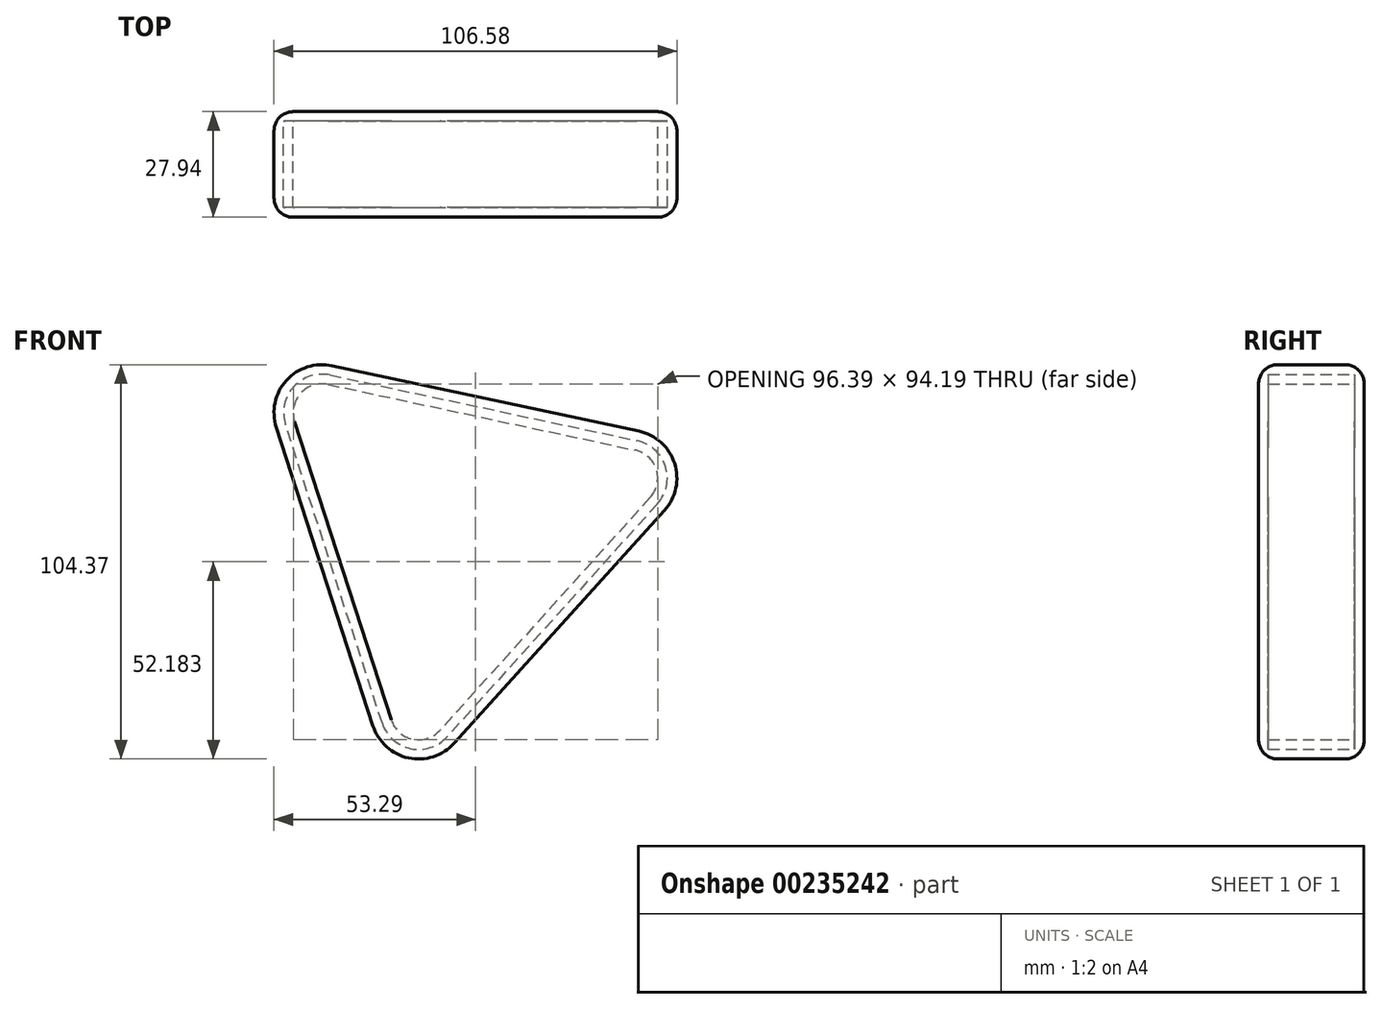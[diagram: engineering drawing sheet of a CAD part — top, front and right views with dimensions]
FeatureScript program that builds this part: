
annotation { "Feature Type Name" : "Feature", "Feature Type Description" : "" }
export const myFeature = defineFeature(function(context is Context, id is Id, definition is map)
    precondition{}
    {
        {
            var Q0;
            Q0=qCreatedBy(makeId("Front.planeOp"),FACE);
            var sketch = newSketch(context, id + "F6", { "sketchPlane" : qUnion([Q0])});
            skCircle(sketch, "E0.cCircle", {"center": v(0, 0) * mm, "radius": 36.66 * mm, "construction": true});
            skLineSegment(sketch, "E0.0", {"start": v(69.76, 22.57) * mm, "end": v(-15.33, -71.7) * mm});
            skLineSegment(sketch, "E0.1", {"start": v(-15.33, -71.7) * mm, "end": v(-54.43, 49.13) * mm});
            skLineSegment(sketch, "E0.2", {"start": v(-54.43, 49.13) * mm, "end": v(69.76, 22.57) * mm});
            skPoint(sketch, "E0.0.midPoint", {"position": v(27.22, -24.56) * mm});
            skSolve(sketch);
        }
        {
            var Q0;
            Q0=makeQuery(id+"F6.imprint","IMPRINT",FACE,{"disambiguationData":[TD([[makeQuery(id+"F6.imprint","IMPRINT",EDGE,{"derivedFrom":sQuery(id+"F6.wireOp",EDGE,"E0.0")}),-1.0]])]});
            extrude(context, id + "F0", {"entities" : qUnion([Q0]), "depth" : 25.4 * mm});
        }
        {
            var Q0;
            Q0=makeQuery(id+"F0.opExtrude","SWEPT_EDGE",EDGE,{"disambiguationData":[OSD([sQuery(id+"F6.wireOp",EDGE,"E0.0"),sQuery(id+"F6.wireOp",EDGE,"E0.2")])]});
            var Q1;
            Q1=makeQuery(id+"F0.opExtrude","SWEPT_EDGE",EDGE,{"disambiguationData":[OSD([sQuery(id+"F6.wireOp",EDGE,"E0.0"),sQuery(id+"F6.wireOp",EDGE,"E0.1")])]});
            var Q2;
            Q2=makeQuery(id+"F0.opExtrude","SWEPT_EDGE",EDGE,{"disambiguationData":[OSD([sQuery(id+"F6.wireOp",EDGE,"E0.1"),sQuery(id+"F6.wireOp",EDGE,"E0.2")])]});
            fillet(context, id + "F1", {"entities" : qUnion([Q0, Q1, Q2]), "radius" : 12.7 * mm, "tangentPropagation" : true, "allowEdgeOverflow" : false});
        }
        {
            var Q0;
            Q0=makeQuery(id+"F0.opExtrude","CAP_FACE",FACE,{"disambiguationData":[OSD([sQuery(id+"F6.wireOp",EDGE,"E0.0"),sQuery(id+"F6.wireOp",EDGE,"E0.1"),sQuery(id+"F6.wireOp",EDGE,"E0.2")])],"isStart":false});
            shell(context, id + "F2", {"entities" : qUnion([Q0]), "thickness" : 2.54 * mm});
        }
        {
            var Q0;
            Q0=makeQuery(id+"F2.opShell","OFFSET_FACE",FACE,{"disambiguationData":[OSD([sQuery(id+"F6.wireOp",EDGE,"E0.0"),sQuery(id+"F6.wireOp",EDGE,"E0.1"),sQuery(id+"F6.wireOp",EDGE,"E0.2")])]});
            var sketch = newSketch(context, id + "F3", { "sketchPlane" : qUnion([Q0])});
            skArc(sketch, "E1.0", {"start": v(-42.83, 29.76) * mm, "mid": v(-41.23, 37.22) * mm, "end": v(-33.98, 39.56) * mm});
            skArc(sketch, "E1.1", {"start": v(47.19, 22.2) * mm, "mid": v(52.85, 17.1) * mm, "end": v(51.25, 9.65) * mm});
            skLineSegment(sketch, "E1.2", {"start": v(51.25, 9.65) * mm, "end": v(-4.36, -51.97) * mm});
            skLineSegment(sketch, "E1.3", {"start": v(-33.98, 39.56) * mm, "end": v(47.19, 22.2) * mm});
            skArc(sketch, "E1.4", {"start": v(-4.36, -51.97) * mm, "mid": v(-11.61, -54.32) * mm, "end": v(-17.27, -49.21) * mm});
            skLineSegment(sketch, "E1.5", {"start": v(-17.27, -49.21) * mm, "end": v(-42.83, 29.76) * mm});
            skSolve(sketch);
        }
        {
            var Q0;
            Q0=makeQuery(id+"F3.imprint","IMPRINT",FACE,{"disambiguationData":[TD([[makeQuery(id+"F3.imprint","IMPRINT",EDGE,{"derivedFrom":sQuery(id+"F3.wireOp",EDGE,"E1.0")}),1.0]])]});
            extrude(context, id + "F4", {"entities" : qUnion([Q0]), "operationType" : NewBodyOperationType.ADD, "depth" : 12.7 * mm});
        }
        {
            var Q0;
            Q0=makeQuery(id+"F4.opExtrude","CAP_FACE",FACE,{"disambiguationData":[OSD([sQuery(id+"F6.wireOp",EDGE,"E0.0"),sQuery(id+"F6.wireOp",EDGE,"E0.1"),sQuery(id+"F6.wireOp",EDGE,"E0.2"),sQuery(id+"F3.wireOp",EDGE,"E1.0"),sQuery(id+"F3.wireOp",EDGE,"E1.1"),sQuery(id+"F3.wireOp",EDGE,"E1.2"),sQuery(id+"F3.wireOp",EDGE,"E1.3"),sQuery(id+"F3.wireOp",EDGE,"E1.4"),sQuery(id+"F3.wireOp",EDGE,"E1.5")])],"isStart":false});
            extrude(context, id + "F7", {"entities" : qUnion([Q0]), "depth" : 10.16 * mm});
        }
        {
            var Q0;
            Q0=makeQuery(id+"F7.opExtrude","CAP_FACE",FACE,{"disambiguationData":[OSD([sQuery(id+"F6.wireOp",EDGE,"E0.0"),sQuery(id+"F6.wireOp",EDGE,"E0.1"),sQuery(id+"F6.wireOp",EDGE,"E0.2"),sQuery(id+"F3.wireOp",EDGE,"E1.0"),sQuery(id+"F3.wireOp",EDGE,"E1.1"),sQuery(id+"F3.wireOp",EDGE,"E1.2"),sQuery(id+"F3.wireOp",EDGE,"E1.3"),sQuery(id+"F3.wireOp",EDGE,"E1.4"),sQuery(id+"F3.wireOp",EDGE,"E1.5")])],"isStart":false});
            var sketch = newSketch(context, id + "F8", { "sketchPlane" : qUnion([Q0])});
            skLineSegment(sketch, "E2.0.0", {"start": v(48.25, 27.17) * mm, "end": v(-32.92, 44.53) * mm});
            skArc(sketch, "E2.0.1", {"start": v(-32.92, 44.53) * mm, "mid": v(-45, 40.62) * mm, "end": v(-47.66, 28.2) * mm});
            skLineSegment(sketch, "E2.0.2", {"start": v(-47.66, 28.2) * mm, "end": v(-22.1, -50.77) * mm});
            skArc(sketch, "E2.0.3", {"start": v(-22.1, -50.77) * mm, "mid": v(-12.68, -59.28) * mm, "end": v(-0.6, -55.37) * mm});
            skLineSegment(sketch, "E2.0.4", {"start": v(-0.6, -55.37) * mm, "end": v(55.02, 6.24) * mm});
            skArc(sketch, "E2.0.5", {"start": v(55.02, 6.24) * mm, "mid": v(57.68, 18.66) * mm, "end": v(48.25, 27.17) * mm});
            skSolve(sketch);
        }
        {
            var Q0;
            Q0 = qSketchRegion(id + "F8", true);
            extrude(context, id + "F9", {"entities" : qUnion([Q0]), "operationType" : NewBodyOperationType.ADD, "depth" : 2.54 * mm});
        }
        {
            var Q0;
            Q0=makeQuery(id+"F9.opExtrude","SWEPT_FACE",FACE,{"disambiguationData":[OSD([sQuery(id+"F8.wireOp",EDGE,"E2.0.0")])]});
            fillet(context, id + "F5", {"entities" : qUnion([Q0]), "radius" : 5.08 * mm, "tangentPropagation" : true, "allowEdgeOverflow" : false});
        }
    });
